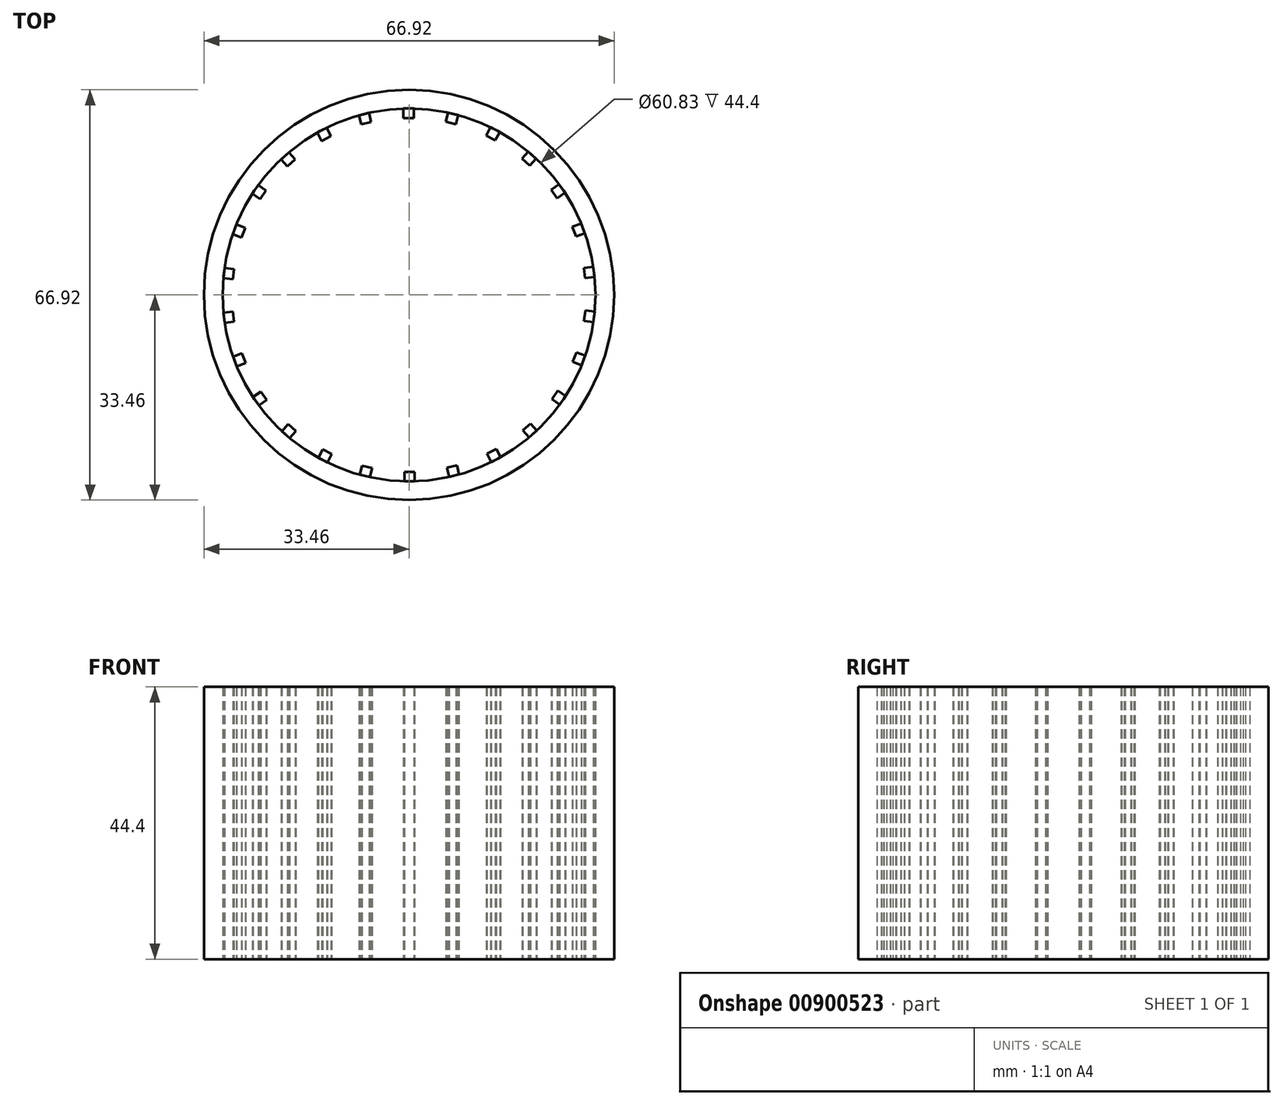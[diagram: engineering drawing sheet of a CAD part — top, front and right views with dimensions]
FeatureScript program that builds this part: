
annotation { "Feature Type Name" : "Feature", "Feature Type Description" : "" }
export const myFeature = defineFeature(function(context is Context, id is Id, definition is map)
    precondition{}
    {
        {
            var Q0;
            Q0=qCreatedBy(makeId("Top.planeOp"),FACE);
            var sketch = newSketch(context, id + "F0", { "sketchPlane" : qUnion([Q0])});
            skCircle(sketch, "E0", {"center": v(0, 0) * mm, "radius": 45.22 * mm});
            skCircle(sketch, "E1", {"center": v(0, 0) * mm, "radius": 41.1 * mm});
            skLineSegment(sketch, "E2.bottom", {"start": v(-1.25, 41.08) * mm, "end": v(1.03, 41.08) * mm});
            skLineSegment(sketch, "E2.top", {"start": v(-1.25, 39) * mm, "end": v(1.03, 39) * mm});
            skLineSegment(sketch, "E2.left", {"start": v(-1.25, 41.08) * mm, "end": v(-1.25, 39) * mm});
            skLineSegment(sketch, "E2.right", {"start": v(1.03, 41.08) * mm, "end": v(1.03, 39) * mm});
            skLineSegment(sketch, "E3.1.0", {"start": v(-11.05, 39.59) * mm, "end": v(-10.55, 37.57) * mm});
            skLineSegment(sketch, "E3.1.1", {"start": v(-8.84, 40.13) * mm, "end": v(-8.34, 38.11) * mm});
            skLineSegment(sketch, "E3.1.2", {"start": v(-10.55, 37.57) * mm, "end": v(-8.34, 38.11) * mm});
            skLineSegment(sketch, "E3.1.3", {"start": v(-11.05, 39.59) * mm, "end": v(-8.84, 40.13) * mm});
            skLineSegment(sketch, "E3.2.0", {"start": v(-20.2, 35.8) * mm, "end": v(-19.23, 33.95) * mm});
            skLineSegment(sketch, "E3.2.1", {"start": v(-18.18, 36.85) * mm, "end": v(-17.22, 35) * mm});
            skLineSegment(sketch, "E3.2.2", {"start": v(-19.23, 33.95) * mm, "end": v(-17.22, 35) * mm});
            skLineSegment(sketch, "E3.2.3", {"start": v(-20.2, 35.8) * mm, "end": v(-18.18, 36.85) * mm});
            skLineSegment(sketch, "E3.3.0", {"start": v(-28.18, 29.92) * mm, "end": v(-26.8, 28.36) * mm});
            skLineSegment(sketch, "E3.3.1", {"start": v(-26.47, 31.43) * mm, "end": v(-25.1, 29.87) * mm});
            skLineSegment(sketch, "E3.3.2", {"start": v(-26.8, 28.36) * mm, "end": v(-25.1, 29.87) * mm});
            skLineSegment(sketch, "E3.3.3", {"start": v(-28.18, 29.92) * mm, "end": v(-26.47, 31.43) * mm});
            skLineSegment(sketch, "E3.4.0", {"start": v(-34.52, 22.3) * mm, "end": v(-32.8, 21.12) * mm});
            skLineSegment(sketch, "E3.4.1", {"start": v(-33.23, 24.18) * mm, "end": v(-31.51, 23) * mm});
            skLineSegment(sketch, "E3.4.2", {"start": v(-32.8, 21.12) * mm, "end": v(-31.51, 23) * mm});
            skLineSegment(sketch, "E3.4.3", {"start": v(-34.52, 22.3) * mm, "end": v(-33.23, 24.18) * mm});
            skLineSegment(sketch, "E3.5.0", {"start": v(-38.85, 13.4) * mm, "end": v(-36.91, 12.66) * mm});
            skLineSegment(sketch, "E3.5.1", {"start": v(-38.05, 15.53) * mm, "end": v(-36.1, 14.79) * mm});
            skLineSegment(sketch, "E3.5.2", {"start": v(-36.91, 12.66) * mm, "end": v(-36.1, 14.79) * mm});
            skLineSegment(sketch, "E3.5.3", {"start": v(-38.85, 13.4) * mm, "end": v(-38.05, 15.53) * mm});
            skLineSegment(sketch, "E3.6.0", {"start": v(-40.93, 3.7) * mm, "end": v(-38.87, 3.46) * mm});
            skLineSegment(sketch, "E3.6.1", {"start": v(-40.66, 5.97) * mm, "end": v(-38.6, 5.72) * mm});
            skLineSegment(sketch, "E3.6.2", {"start": v(-38.87, 3.46) * mm, "end": v(-38.6, 5.72) * mm});
            skLineSegment(sketch, "E3.6.3", {"start": v(-40.93, 3.7) * mm, "end": v(-40.66, 5.97) * mm});
            skLineSegment(sketch, "E3.7.0", {"start": v(-40.63, -6.2) * mm, "end": v(-38.56, -5.95) * mm});
            skLineSegment(sketch, "E3.7.1", {"start": v(-40.9, -3.93) * mm, "end": v(-38.84, -3.68) * mm});
            skLineSegment(sketch, "E3.7.2", {"start": v(-38.56, -5.95) * mm, "end": v(-38.84, -3.68) * mm});
            skLineSegment(sketch, "E3.7.3", {"start": v(-40.63, -6.2) * mm, "end": v(-40.9, -3.93) * mm});
            skLineSegment(sketch, "E3.8.0", {"start": v(-37.97, -15.74) * mm, "end": v(-36.02, -15) * mm});
            skLineSegment(sketch, "E3.8.1", {"start": v(-38.77, -13.6) * mm, "end": v(-36.83, -12.87) * mm});
            skLineSegment(sketch, "E3.8.2", {"start": v(-36.02, -15) * mm, "end": v(-36.83, -12.87) * mm});
            skLineSegment(sketch, "E3.8.3", {"start": v(-37.97, -15.74) * mm, "end": v(-38.77, -13.6) * mm});
            skLineSegment(sketch, "E3.9.0", {"start": v(-33.1, -24.37) * mm, "end": v(-31.38, -23.19) * mm});
            skLineSegment(sketch, "E3.9.1", {"start": v(-34.4, -22.5) * mm, "end": v(-32.68, -21.31) * mm});
            skLineSegment(sketch, "E3.9.2", {"start": v(-31.38, -23.19) * mm, "end": v(-32.68, -21.31) * mm});
            skLineSegment(sketch, "E3.9.3", {"start": v(-33.1, -24.37) * mm, "end": v(-34.4, -22.5) * mm});
            skLineSegment(sketch, "E3.10.0", {"start": v(-26.3, -31.58) * mm, "end": v(-24.92, -30.02) * mm});
            skLineSegment(sketch, "E3.10.1", {"start": v(-28, -30.07) * mm, "end": v(-26.63, -28.51) * mm});
            skLineSegment(sketch, "E3.10.2", {"start": v(-24.92, -30.02) * mm, "end": v(-26.63, -28.51) * mm});
            skLineSegment(sketch, "E3.10.3", {"start": v(-26.3, -31.58) * mm, "end": v(-28, -30.07) * mm});
            skLineSegment(sketch, "E3.11.0", {"start": v(-17.98, -36.96) * mm, "end": v(-17.01, -35.12) * mm});
            skLineSegment(sketch, "E3.11.1", {"start": v(-20, -35.9) * mm, "end": v(-19.03, -34.06) * mm});
            skLineSegment(sketch, "E3.11.2", {"start": v(-17.01, -35.12) * mm, "end": v(-19.03, -34.06) * mm});
            skLineSegment(sketch, "E3.11.3", {"start": v(-17.98, -36.96) * mm, "end": v(-20, -35.9) * mm});
            skLineSegment(sketch, "E3.12.0", {"start": v(-8.61, -40.19) * mm, "end": v(-8.12, -38.17) * mm});
            skLineSegment(sketch, "E3.12.1", {"start": v(-10.83, -39.64) * mm, "end": v(-10.33, -37.62) * mm});
            skLineSegment(sketch, "E3.12.2", {"start": v(-8.12, -38.17) * mm, "end": v(-10.33, -37.62) * mm});
            skLineSegment(sketch, "E3.12.3", {"start": v(-8.61, -40.19) * mm, "end": v(-10.83, -39.64) * mm});
            skLineSegment(sketch, "E3.13.0", {"start": v(1.25, -41.08) * mm, "end": v(1.25, -39) * mm});
            skLineSegment(sketch, "E3.13.1", {"start": v(-1.03, -41.08) * mm, "end": v(-1.03, -39) * mm});
            skLineSegment(sketch, "E3.13.2", {"start": v(1.25, -39) * mm, "end": v(-1.03, -39) * mm});
            skLineSegment(sketch, "E3.13.3", {"start": v(1.25, -41.08) * mm, "end": v(-1.03, -41.08) * mm});
            skLineSegment(sketch, "E3.14.0", {"start": v(11.05, -39.59) * mm, "end": v(10.55, -37.57) * mm});
            skLineSegment(sketch, "E3.14.1", {"start": v(8.84, -40.13) * mm, "end": v(8.34, -38.11) * mm});
            skLineSegment(sketch, "E3.14.2", {"start": v(10.55, -37.57) * mm, "end": v(8.34, -38.11) * mm});
            skLineSegment(sketch, "E3.14.3", {"start": v(11.05, -39.59) * mm, "end": v(8.84, -40.13) * mm});
            skLineSegment(sketch, "E3.15.0", {"start": v(20.2, -35.8) * mm, "end": v(19.23, -33.95) * mm});
            skLineSegment(sketch, "E3.15.1", {"start": v(18.18, -36.85) * mm, "end": v(17.22, -35) * mm});
            skLineSegment(sketch, "E3.15.2", {"start": v(19.23, -33.95) * mm, "end": v(17.22, -35) * mm});
            skLineSegment(sketch, "E3.15.3", {"start": v(20.2, -35.8) * mm, "end": v(18.18, -36.85) * mm});
            skLineSegment(sketch, "E3.16.0", {"start": v(28.18, -29.92) * mm, "end": v(26.8, -28.36) * mm});
            skLineSegment(sketch, "E3.16.1", {"start": v(26.47, -31.43) * mm, "end": v(25.1, -29.87) * mm});
            skLineSegment(sketch, "E3.16.2", {"start": v(26.8, -28.36) * mm, "end": v(25.1, -29.87) * mm});
            skLineSegment(sketch, "E3.16.3", {"start": v(28.18, -29.92) * mm, "end": v(26.47, -31.43) * mm});
            skLineSegment(sketch, "E3.17.0", {"start": v(34.52, -22.3) * mm, "end": v(32.8, -21.12) * mm});
            skLineSegment(sketch, "E3.17.1", {"start": v(33.23, -24.18) * mm, "end": v(31.51, -23) * mm});
            skLineSegment(sketch, "E3.17.2", {"start": v(32.8, -21.12) * mm, "end": v(31.51, -23) * mm});
            skLineSegment(sketch, "E3.17.3", {"start": v(34.52, -22.3) * mm, "end": v(33.23, -24.18) * mm});
            skLineSegment(sketch, "E3.18.0", {"start": v(38.85, -13.4) * mm, "end": v(36.91, -12.66) * mm});
            skLineSegment(sketch, "E3.18.1", {"start": v(38.05, -15.53) * mm, "end": v(36.1, -14.79) * mm});
            skLineSegment(sketch, "E3.18.2", {"start": v(36.91, -12.66) * mm, "end": v(36.1, -14.79) * mm});
            skLineSegment(sketch, "E3.18.3", {"start": v(38.85, -13.4) * mm, "end": v(38.05, -15.53) * mm});
            skLineSegment(sketch, "E3.19.0", {"start": v(40.93, -3.7) * mm, "end": v(38.87, -3.46) * mm});
            skLineSegment(sketch, "E3.19.1", {"start": v(40.66, -5.97) * mm, "end": v(38.6, -5.72) * mm});
            skLineSegment(sketch, "E3.19.2", {"start": v(38.87, -3.46) * mm, "end": v(38.6, -5.72) * mm});
            skLineSegment(sketch, "E3.19.3", {"start": v(40.93, -3.7) * mm, "end": v(40.66, -5.97) * mm});
            skLineSegment(sketch, "E3.20.0", {"start": v(40.63, 6.2) * mm, "end": v(38.56, 5.95) * mm});
            skLineSegment(sketch, "E3.20.1", {"start": v(40.9, 3.93) * mm, "end": v(38.84, 3.68) * mm});
            skLineSegment(sketch, "E3.20.2", {"start": v(38.56, 5.95) * mm, "end": v(38.84, 3.68) * mm});
            skLineSegment(sketch, "E3.20.3", {"start": v(40.63, 6.2) * mm, "end": v(40.9, 3.93) * mm});
            skLineSegment(sketch, "E3.21.0", {"start": v(37.97, 15.74) * mm, "end": v(36.02, 15) * mm});
            skLineSegment(sketch, "E3.21.1", {"start": v(38.77, 13.6) * mm, "end": v(36.83, 12.87) * mm});
            skLineSegment(sketch, "E3.21.2", {"start": v(36.02, 15) * mm, "end": v(36.83, 12.87) * mm});
            skLineSegment(sketch, "E3.21.3", {"start": v(37.97, 15.74) * mm, "end": v(38.77, 13.6) * mm});
            skLineSegment(sketch, "E3.22.0", {"start": v(33.1, 24.37) * mm, "end": v(31.38, 23.19) * mm});
            skLineSegment(sketch, "E3.22.1", {"start": v(34.4, 22.5) * mm, "end": v(32.68, 21.31) * mm});
            skLineSegment(sketch, "E3.22.2", {"start": v(31.38, 23.19) * mm, "end": v(32.68, 21.31) * mm});
            skLineSegment(sketch, "E3.22.3", {"start": v(33.1, 24.37) * mm, "end": v(34.4, 22.5) * mm});
            skLineSegment(sketch, "E3.23.0", {"start": v(26.3, 31.58) * mm, "end": v(24.92, 30.02) * mm});
            skLineSegment(sketch, "E3.23.1", {"start": v(28, 30.07) * mm, "end": v(26.63, 28.51) * mm});
            skLineSegment(sketch, "E3.23.2", {"start": v(24.92, 30.02) * mm, "end": v(26.63, 28.51) * mm});
            skLineSegment(sketch, "E3.23.3", {"start": v(26.3, 31.58) * mm, "end": v(28, 30.07) * mm});
            skLineSegment(sketch, "E3.24.0", {"start": v(17.98, 36.96) * mm, "end": v(17.01, 35.12) * mm});
            skLineSegment(sketch, "E3.24.1", {"start": v(20, 35.9) * mm, "end": v(19.03, 34.06) * mm});
            skLineSegment(sketch, "E3.24.2", {"start": v(17.01, 35.12) * mm, "end": v(19.03, 34.06) * mm});
            skLineSegment(sketch, "E3.24.3", {"start": v(17.98, 36.96) * mm, "end": v(20, 35.9) * mm});
            skLineSegment(sketch, "E3.25.0", {"start": v(8.61, 40.19) * mm, "end": v(8.12, 38.17) * mm});
            skLineSegment(sketch, "E3.25.1", {"start": v(10.83, 39.64) * mm, "end": v(10.33, 37.62) * mm});
            skLineSegment(sketch, "E3.25.2", {"start": v(8.12, 38.17) * mm, "end": v(10.33, 37.62) * mm});
            skLineSegment(sketch, "E3.25.3", {"start": v(8.61, 40.19) * mm, "end": v(10.83, 39.64) * mm});
            skSolve(sketch);
        }
        {
            var Q0;
            Q0=makeQuery(id+"F0.imprint","IMPRINT",FACE,{"disambiguationData":[TD([[makeQuery(id+"F0.imprint","IMPRINT",EDGE,{"derivedFrom":sQuery(id+"F0.wireOp",EDGE,"E3.1.0")}),1.0]])]});
            var Q1;
            Q1=makeQuery(id+"F0.imprint","IMPRINT",FACE,{"disambiguationData":[TD([[makeQuery(id+"F0.imprint","IMPRINT",EDGE,{"derivedFrom":sQuery(id+"F0.wireOp",EDGE,"E2.bottom")}),-1.0]])]});
            var Q2;
            Q2=makeQuery(id+"F0.imprint","IMPRINT",FACE,{"disambiguationData":[TD([[makeQuery(id+"F0.imprint","IMPRINT",EDGE,{"derivedFrom":sQuery(id+"F0.wireOp",EDGE,"E3.25.0")}),1.0]])]});
            var Q3;
            Q3=makeQuery(id+"F0.imprint","IMPRINT",FACE,{"disambiguationData":[TD([[makeQuery(id+"F0.imprint","IMPRINT",EDGE,{"derivedFrom":sQuery(id+"F0.wireOp",EDGE,"E3.24.0")}),1.0]])]});
            var Q4;
            Q4=makeQuery(id+"F0.imprint","IMPRINT",FACE,{"disambiguationData":[TD([[makeQuery(id+"F0.imprint","IMPRINT",EDGE,{"derivedFrom":sQuery(id+"F0.wireOp",EDGE,"E0")}),1.0]])]});
            var Q5;
            Q5=makeQuery(id+"F0.imprint","IMPRINT",FACE,{"disambiguationData":[TD([[makeQuery(id+"F0.imprint","IMPRINT",EDGE,{"derivedFrom":sQuery(id+"F0.wireOp",EDGE,"E3.23.0")}),1.0]])]});
            var Q6;
            Q6=makeQuery(id+"F0.imprint","IMPRINT",FACE,{"disambiguationData":[TD([[makeQuery(id+"F0.imprint","IMPRINT",EDGE,{"derivedFrom":sQuery(id+"F0.wireOp",EDGE,"E3.22.0")}),1.0]])]});
            var Q7;
            Q7=makeQuery(id+"F0.imprint","IMPRINT",FACE,{"disambiguationData":[TD([[makeQuery(id+"F0.imprint","IMPRINT",EDGE,{"derivedFrom":sQuery(id+"F0.wireOp",EDGE,"E3.21.0")}),1.0]])]});
            var Q8;
            Q8=makeQuery(id+"F0.imprint","IMPRINT",FACE,{"disambiguationData":[TD([[makeQuery(id+"F0.imprint","IMPRINT",EDGE,{"derivedFrom":sQuery(id+"F0.wireOp",EDGE,"E3.20.0")}),1.0]])]});
            var Q9;
            Q9=makeQuery(id+"F0.imprint","IMPRINT",FACE,{"disambiguationData":[TD([[makeQuery(id+"F0.imprint","IMPRINT",EDGE,{"derivedFrom":sQuery(id+"F0.wireOp",EDGE,"E3.19.0")}),1.0]])]});
            var Q10;
            Q10=makeQuery(id+"F0.imprint","IMPRINT",FACE,{"disambiguationData":[TD([[makeQuery(id+"F0.imprint","IMPRINT",EDGE,{"derivedFrom":sQuery(id+"F0.wireOp",EDGE,"E3.18.0")}),1.0]])]});
            var Q11;
            Q11=makeQuery(id+"F0.imprint","IMPRINT",FACE,{"disambiguationData":[TD([[makeQuery(id+"F0.imprint","IMPRINT",EDGE,{"derivedFrom":sQuery(id+"F0.wireOp",EDGE,"E3.17.0")}),1.0]])]});
            var Q12;
            Q12=makeQuery(id+"F0.imprint","IMPRINT",FACE,{"disambiguationData":[TD([[makeQuery(id+"F0.imprint","IMPRINT",EDGE,{"derivedFrom":sQuery(id+"F0.wireOp",EDGE,"E3.16.0")}),1.0]])]});
            var Q13;
            Q13=makeQuery(id+"F0.imprint","IMPRINT",FACE,{"disambiguationData":[TD([[makeQuery(id+"F0.imprint","IMPRINT",EDGE,{"derivedFrom":sQuery(id+"F0.wireOp",EDGE,"E3.15.0")}),1.0]])]});
            var Q14;
            Q14=makeQuery(id+"F0.imprint","IMPRINT",FACE,{"disambiguationData":[TD([[makeQuery(id+"F0.imprint","IMPRINT",EDGE,{"derivedFrom":sQuery(id+"F0.wireOp",EDGE,"E3.14.0")}),1.0]])]});
            var Q15;
            Q15=makeQuery(id+"F0.imprint","IMPRINT",FACE,{"disambiguationData":[TD([[makeQuery(id+"F0.imprint","IMPRINT",EDGE,{"derivedFrom":sQuery(id+"F0.wireOp",EDGE,"E3.13.0")}),1.0]])]});
            var Q16;
            Q16=makeQuery(id+"F0.imprint","IMPRINT",FACE,{"disambiguationData":[TD([[makeQuery(id+"F0.imprint","IMPRINT",EDGE,{"derivedFrom":sQuery(id+"F0.wireOp",EDGE,"E3.12.0")}),1.0]])]});
            var Q17;
            Q17=makeQuery(id+"F0.imprint","IMPRINT",FACE,{"disambiguationData":[TD([[makeQuery(id+"F0.imprint","IMPRINT",EDGE,{"derivedFrom":sQuery(id+"F0.wireOp",EDGE,"E3.11.0")}),1.0]])]});
            var Q18;
            Q18=makeQuery(id+"F0.imprint","IMPRINT",FACE,{"disambiguationData":[TD([[makeQuery(id+"F0.imprint","IMPRINT",EDGE,{"derivedFrom":sQuery(id+"F0.wireOp",EDGE,"E3.2.0")}),1.0]])]});
            var Q19;
            Q19=makeQuery(id+"F0.imprint","IMPRINT",FACE,{"disambiguationData":[TD([[makeQuery(id+"F0.imprint","IMPRINT",EDGE,{"derivedFrom":sQuery(id+"F0.wireOp",EDGE,"E3.3.0")}),1.0]])]});
            var Q20;
            Q20=makeQuery(id+"F0.imprint","IMPRINT",FACE,{"disambiguationData":[TD([[makeQuery(id+"F0.imprint","IMPRINT",EDGE,{"derivedFrom":sQuery(id+"F0.wireOp",EDGE,"E3.4.0")}),1.0]])]});
            var Q21;
            Q21=makeQuery(id+"F0.imprint","IMPRINT",FACE,{"disambiguationData":[TD([[makeQuery(id+"F0.imprint","IMPRINT",EDGE,{"derivedFrom":sQuery(id+"F0.wireOp",EDGE,"E3.5.0")}),1.0]])]});
            var Q22;
            Q22=makeQuery(id+"F0.imprint","IMPRINT",FACE,{"disambiguationData":[TD([[makeQuery(id+"F0.imprint","IMPRINT",EDGE,{"derivedFrom":sQuery(id+"F0.wireOp",EDGE,"E3.6.0")}),1.0]])]});
            var Q23;
            Q23=makeQuery(id+"F0.imprint","IMPRINT",FACE,{"disambiguationData":[TD([[makeQuery(id+"F0.imprint","IMPRINT",EDGE,{"derivedFrom":sQuery(id+"F0.wireOp",EDGE,"E3.7.0")}),1.0]])]});
            var Q24;
            Q24=makeQuery(id+"F0.imprint","IMPRINT",FACE,{"disambiguationData":[TD([[makeQuery(id+"F0.imprint","IMPRINT",EDGE,{"derivedFrom":sQuery(id+"F0.wireOp",EDGE,"E3.8.0")}),1.0]])]});
            var Q25;
            Q25=makeQuery(id+"F0.imprint","IMPRINT",FACE,{"disambiguationData":[TD([[makeQuery(id+"F0.imprint","IMPRINT",EDGE,{"derivedFrom":sQuery(id+"F0.wireOp",EDGE,"E3.9.0")}),1.0]])]});
            var Q26;
            Q26=makeQuery(id+"F0.imprint","IMPRINT",FACE,{"disambiguationData":[TD([[makeQuery(id+"F0.imprint","IMPRINT",EDGE,{"derivedFrom":sQuery(id+"F0.wireOp",EDGE,"E3.10.0")}),1.0]])]});
            extrude(context, id + "F1", {"entities" : qUnion([Q0, Q1, Q2, Q3, Q4, Q5, Q6, Q7, Q8, Q9, Q10, Q11, Q12, Q13, Q14, Q15, Q16, Q17, Q18, Q19, Q20, Q21, Q22, Q23, Q24, Q25, Q26]), "depth" : 60 * mm, "offsetDistance" : 25 * mm});
        }
        {
            var Q0;
            Q0=makeQuery(id+"F1.opExtrude","SWEPT_BODY",BODY,{"disambiguationData":[OSD([sQuery(id+"F0.wireOp",EDGE,"E3.1.0"),sQuery(id+"F0.wireOp",EDGE,"E3.1.1"),sQuery(id+"F0.wireOp",EDGE,"E3.1.2"),sQuery(id+"F0.wireOp",EDGE,"E3.1.3")])]});
            var Q1;
            Q1=makeQuery(id+"F1.opExtrude","SWEPT_BODY",BODY,{"disambiguationData":[OSD([sQuery(id+"F0.wireOp",EDGE,"E3.12.0"),sQuery(id+"F0.wireOp",EDGE,"E3.12.1"),sQuery(id+"F0.wireOp",EDGE,"E3.12.2"),sQuery(id+"F0.wireOp",EDGE,"E3.12.3")])]});
            var Q2;
            Q2=makeQuery(id+"F1.opExtrude","SWEPT_BODY",BODY,{"disambiguationData":[OSD([sQuery(id+"F0.wireOp",EDGE,"E3.14.0"),sQuery(id+"F0.wireOp",EDGE,"E3.14.1"),sQuery(id+"F0.wireOp",EDGE,"E3.14.2"),sQuery(id+"F0.wireOp",EDGE,"E3.14.3")])]});
            var Q3;
            Q3=makeQuery(id+"F1.opExtrude","SWEPT_BODY",BODY,{"disambiguationData":[OSD([sQuery(id+"F0.wireOp",EDGE,"E3.16.0"),sQuery(id+"F0.wireOp",EDGE,"E3.16.1"),sQuery(id+"F0.wireOp",EDGE,"E3.16.2"),sQuery(id+"F0.wireOp",EDGE,"E3.16.3")])]});
            var Q4;
            Q4=makeQuery(id+"F1.opExtrude","SWEPT_BODY",BODY,{"disambiguationData":[OSD([sQuery(id+"F0.wireOp",EDGE,"E3.25.0"),sQuery(id+"F0.wireOp",EDGE,"E3.25.1"),sQuery(id+"F0.wireOp",EDGE,"E3.25.2"),sQuery(id+"F0.wireOp",EDGE,"E3.25.3")])]});
            var Q5;
            Q5=makeQuery(id+"F1.opExtrude","SWEPT_BODY",BODY,{"disambiguationData":[OSD([sQuery(id+"F0.wireOp",EDGE,"E3.2.0"),sQuery(id+"F0.wireOp",EDGE,"E3.2.1"),sQuery(id+"F0.wireOp",EDGE,"E3.2.2"),sQuery(id+"F0.wireOp",EDGE,"E3.2.3")])]});
            var Q6;
            Q6=makeQuery(id+"F1.opExtrude","SWEPT_BODY",BODY,{"disambiguationData":[OSD([sQuery(id+"F0.wireOp",EDGE,"E2.bottom"),sQuery(id+"F0.wireOp",EDGE,"E2.top"),sQuery(id+"F0.wireOp",EDGE,"E2.left"),sQuery(id+"F0.wireOp",EDGE,"E2.right")])]});
            var Q7;
            Q7=makeQuery(id+"F1.opExtrude","SWEPT_BODY",BODY,{"disambiguationData":[OSD([sQuery(id+"F0.wireOp",EDGE,"E0"),sQuery(id+"F0.wireOp",EDGE,"E1")])]});
            var Q8;
            Q8=makeQuery(id+"F1.opExtrude","SWEPT_BODY",BODY,{"disambiguationData":[OSD([sQuery(id+"F0.wireOp",EDGE,"E3.23.0"),sQuery(id+"F0.wireOp",EDGE,"E3.23.1"),sQuery(id+"F0.wireOp",EDGE,"E3.23.2"),sQuery(id+"F0.wireOp",EDGE,"E3.23.3")])]});
            var Q9;
            Q9=makeQuery(id+"F1.opExtrude","SWEPT_BODY",BODY,{"disambiguationData":[OSD([sQuery(id+"F0.wireOp",EDGE,"E3.5.0"),sQuery(id+"F0.wireOp",EDGE,"E3.5.1"),sQuery(id+"F0.wireOp",EDGE,"E3.5.2"),sQuery(id+"F0.wireOp",EDGE,"E3.5.3")])]});
            var Q10;
            Q10=makeQuery(id+"F1.opExtrude","SWEPT_BODY",BODY,{"disambiguationData":[OSD([sQuery(id+"F0.wireOp",EDGE,"E3.19.0"),sQuery(id+"F0.wireOp",EDGE,"E3.19.1"),sQuery(id+"F0.wireOp",EDGE,"E3.19.2"),sQuery(id+"F0.wireOp",EDGE,"E3.19.3")])]});
            var Q11;
            Q11=makeQuery(id+"F1.opExtrude","SWEPT_BODY",BODY,{"disambiguationData":[OSD([sQuery(id+"F0.wireOp",EDGE,"E3.22.0"),sQuery(id+"F0.wireOp",EDGE,"E3.22.1"),sQuery(id+"F0.wireOp",EDGE,"E3.22.2"),sQuery(id+"F0.wireOp",EDGE,"E3.22.3")])]});
            var Q12;
            Q12=makeQuery(id+"F1.opExtrude","SWEPT_BODY",BODY,{"disambiguationData":[OSD([sQuery(id+"F0.wireOp",EDGE,"E3.18.0"),sQuery(id+"F0.wireOp",EDGE,"E3.18.1"),sQuery(id+"F0.wireOp",EDGE,"E3.18.2"),sQuery(id+"F0.wireOp",EDGE,"E3.18.3")])]});
            var Q13;
            Q13=makeQuery(id+"F1.opExtrude","SWEPT_BODY",BODY,{"disambiguationData":[OSD([sQuery(id+"F0.wireOp",EDGE,"E3.13.0"),sQuery(id+"F0.wireOp",EDGE,"E3.13.1"),sQuery(id+"F0.wireOp",EDGE,"E3.13.2"),sQuery(id+"F0.wireOp",EDGE,"E3.13.3")])]});
            var Q14;
            Q14=makeQuery(id+"F1.opExtrude","SWEPT_BODY",BODY,{"disambiguationData":[OSD([sQuery(id+"F0.wireOp",EDGE,"E3.11.0"),sQuery(id+"F0.wireOp",EDGE,"E3.11.1"),sQuery(id+"F0.wireOp",EDGE,"E3.11.2"),sQuery(id+"F0.wireOp",EDGE,"E3.11.3")])]});
            var Q15;
            Q15=makeQuery(id+"F1.opExtrude","SWEPT_BODY",BODY,{"disambiguationData":[OSD([sQuery(id+"F0.wireOp",EDGE,"E3.15.0"),sQuery(id+"F0.wireOp",EDGE,"E3.15.1"),sQuery(id+"F0.wireOp",EDGE,"E3.15.2"),sQuery(id+"F0.wireOp",EDGE,"E3.15.3")])]});
            var Q16;
            Q16=makeQuery(id+"F1.opExtrude","SWEPT_BODY",BODY,{"disambiguationData":[OSD([sQuery(id+"F0.wireOp",EDGE,"E3.8.0"),sQuery(id+"F0.wireOp",EDGE,"E3.8.1"),sQuery(id+"F0.wireOp",EDGE,"E3.8.2"),sQuery(id+"F0.wireOp",EDGE,"E3.8.3")])]});
            var Q17;
            Q17=makeQuery(id+"F1.opExtrude","SWEPT_BODY",BODY,{"disambiguationData":[OSD([sQuery(id+"F0.wireOp",EDGE,"E3.17.0"),sQuery(id+"F0.wireOp",EDGE,"E3.17.1"),sQuery(id+"F0.wireOp",EDGE,"E3.17.2"),sQuery(id+"F0.wireOp",EDGE,"E3.17.3")])]});
            var Q18;
            Q18=makeQuery(id+"F1.opExtrude","SWEPT_BODY",BODY,{"disambiguationData":[OSD([sQuery(id+"F0.wireOp",EDGE,"E3.24.0"),sQuery(id+"F0.wireOp",EDGE,"E3.24.1"),sQuery(id+"F0.wireOp",EDGE,"E3.24.2"),sQuery(id+"F0.wireOp",EDGE,"E3.24.3")])]});
            var Q19;
            Q19=makeQuery(id+"F1.opExtrude","SWEPT_BODY",BODY,{"disambiguationData":[OSD([sQuery(id+"F0.wireOp",EDGE,"E3.3.0"),sQuery(id+"F0.wireOp",EDGE,"E3.3.1"),sQuery(id+"F0.wireOp",EDGE,"E3.3.2"),sQuery(id+"F0.wireOp",EDGE,"E3.3.3")])]});
            var Q20;
            Q20=makeQuery(id+"F1.opExtrude","SWEPT_BODY",BODY,{"disambiguationData":[OSD([sQuery(id+"F0.wireOp",EDGE,"E3.6.0"),sQuery(id+"F0.wireOp",EDGE,"E3.6.1"),sQuery(id+"F0.wireOp",EDGE,"E3.6.2"),sQuery(id+"F0.wireOp",EDGE,"E3.6.3")])]});
            var Q21;
            Q21=makeQuery(id+"F1.opExtrude","SWEPT_BODY",BODY,{"disambiguationData":[OSD([sQuery(id+"F0.wireOp",EDGE,"E3.7.0"),sQuery(id+"F0.wireOp",EDGE,"E3.7.1"),sQuery(id+"F0.wireOp",EDGE,"E3.7.2"),sQuery(id+"F0.wireOp",EDGE,"E3.7.3")])]});
            var Q22;
            Q22=makeQuery(id+"F1.opExtrude","SWEPT_BODY",BODY,{"disambiguationData":[OSD([sQuery(id+"F0.wireOp",EDGE,"E3.10.0"),sQuery(id+"F0.wireOp",EDGE,"E3.10.1"),sQuery(id+"F0.wireOp",EDGE,"E3.10.2"),sQuery(id+"F0.wireOp",EDGE,"E3.10.3")])]});
            var Q23;
            Q23=makeQuery(id+"F1.opExtrude","SWEPT_BODY",BODY,{"disambiguationData":[OSD([sQuery(id+"F0.wireOp",EDGE,"E3.21.0"),sQuery(id+"F0.wireOp",EDGE,"E3.21.1"),sQuery(id+"F0.wireOp",EDGE,"E3.21.2"),sQuery(id+"F0.wireOp",EDGE,"E3.21.3")])]});
            var Q24;
            Q24=makeQuery(id+"F1.opExtrude","SWEPT_BODY",BODY,{"disambiguationData":[OSD([sQuery(id+"F0.wireOp",EDGE,"E3.4.0"),sQuery(id+"F0.wireOp",EDGE,"E3.4.1"),sQuery(id+"F0.wireOp",EDGE,"E3.4.2"),sQuery(id+"F0.wireOp",EDGE,"E3.4.3")])]});
            var Q25;
            Q25=makeQuery(id+"F1.opExtrude","SWEPT_BODY",BODY,{"disambiguationData":[OSD([sQuery(id+"F0.wireOp",EDGE,"E3.9.0"),sQuery(id+"F0.wireOp",EDGE,"E3.9.1"),sQuery(id+"F0.wireOp",EDGE,"E3.9.2"),sQuery(id+"F0.wireOp",EDGE,"E3.9.3")])]});
            var Q26;
            Q26=makeQuery(id+"F1.opExtrude","SWEPT_BODY",BODY,{"disambiguationData":[OSD([sQuery(id+"F0.wireOp",EDGE,"E3.20.0"),sQuery(id+"F0.wireOp",EDGE,"E3.20.1"),sQuery(id+"F0.wireOp",EDGE,"E3.20.2"),sQuery(id+"F0.wireOp",EDGE,"E3.20.3")])]});
            var Q27;
            Q27=qCreatedBy(makeId("Origin.pointOp"),VERTEX);
            transform(context, id + "F2", {"entities" : qUnion([Q0, Q1, Q2, Q3, Q4, Q5, Q6, Q7, Q8, Q9, Q10, Q11, Q12, Q13, Q14, Q15, Q16, Q17, Q18, Q19, Q20, Q21, Q22, Q23, Q24, Q25, Q26]), "transformType" : TransformType.SCALE_UNIFORMLY, "scale" : 0.74, "scalePoint" : qUnion([Q27]), "makeCopy" : false});
        }
    });
